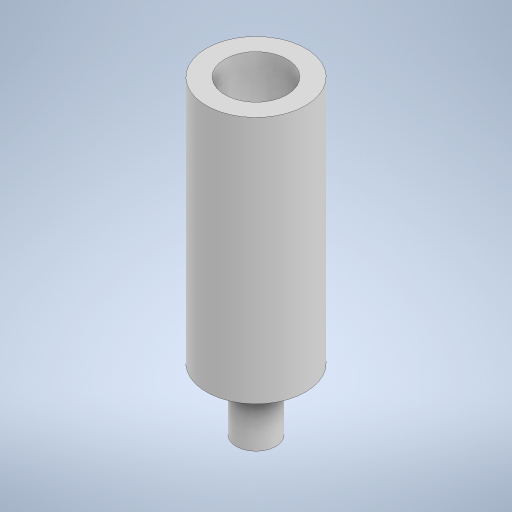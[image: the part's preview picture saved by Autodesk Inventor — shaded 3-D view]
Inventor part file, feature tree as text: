
AUTODESK INVENTOR PART (.ipt)
format: ipt  version: 2024.2 (Build 282272000, 272)  size: 239,104 bytes
history: native  units: mm
features: extrude x3, sketch x3
ambient origin geometry x8: Origin, YZ Plane, XZ Plane, XY Plane, X Axis, Y Axis, Z Axis, Center Point
bodies: Solid1 (feature_tree)
feature tree (6):
  extrude  "Extrusion1"  Depth=5.0mm TaperAngle=0.0deg
  extrude  "Extrusion2"  Depth=20.0mm TaperAngle=0.0deg
  extrude  "Extrusion3"  Depth=5.0mm TaperAngle=0.0deg
  sketch  "Sketch1"  dims[d0=3.2mm d1=5.0mm d2=0.0mm]
  sketch  "Sketch2"  dims[d3=8.0mm d4=20.0mm d5=0.0mm]
  sketch  "Sketch3"  dims[d6=5.0mm d7=5.0mm d8=0.0mm]
